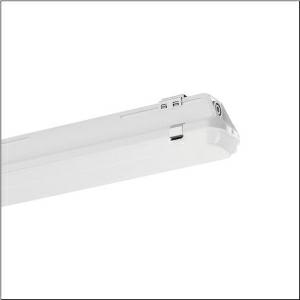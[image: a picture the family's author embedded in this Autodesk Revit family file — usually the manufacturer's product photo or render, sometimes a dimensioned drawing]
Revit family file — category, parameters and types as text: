
# Revit family: monsun_r__21_51fb10dp660b_51d9
name_source: partatom
category: Lighting Fixtures
units: mm (PartAtom-declared; Revit-internal decimal feet)

## family parameters
Cut with Voids When Loaded = No
Host = Face
Light Source = No
Part Type = Normal
Room Calculation Point = No
Round Connector Dimension = Use Diameter
Shared = No

## types (1)
- --- (1 x LED, 6060 lm, 39.4 W, 6500K)
    Apparent Load = 39 VA
    CIE Flux Codes = 47 77 93 94 100
    Color Rendering = 80
    Color Temperature = 6500K
    Default Elevation = 1800 mm
    Description = Monsun® 21, damp-proof luminaire, chain hanger, primary optical cover: enclosure, of PMMA, light emission: direct distribution, primary light characteristic: symmetric, installation type: suspended mounting, surface-mounted, horizontal mounting, vertical mounting, LED, rated luminous flux: 6.060lm, luminous efficacy: 154lm/W, light colour: 865, colour temperature: 6500K, control gear: ECG DALI, with terminal, 5-pole, max. 2.5mm², mains connection: 220..240V, AC, 50/60Hz, rated input power: 39W, housing, of glass-fibre reinforced polyester, uncoated, bright grey, length: 1.590mm, width: 90mm, height: 88mm, clip for enclosure, of stainless steel (V2A), ceiling mounting element, of stainless steel (V2A), chain hanger, of stainless steel (V2A), protection rating (complete): IP66, insulation class (complete): insulation class I (protective earthing), certification: CE, ENEC, VDE, UKCA, protection symbol: D, impact resistance: IK04, permissible operating ambient temperature: -25..+35°C, standard: EN 50419, EN 60598-2-1, corresponds to IFS (International Featured Standards) requirements for safety and quality in the food industry, for indoor or canopied outdoor use, no direct snow, no direct sun, no direct rain, packaging unit: 1 piece
    Height = 89 mm
    Lamp = 1 x LED
    Lamp Light Flux = 6060 lm
    Lamp Power = 39.4 W
    Lamp count = 1
    Length = 1590 mm
    Luminous efficacy = 154 lm/W
    Manufacturer = Siteco
    ModVariant = No
    Model = 51FB10DP660B
    Mounting Place = Ceiling
    Mounting Type = Pendant
    Number of Poles = 1
    OnlyDefault = Yes
    Power Factor = 1
    Product Name = Monsun® 21
    Product group = damp-proof luminaire | ceiling pendant
    ProductGroupID = 908
    Protection Class = Protection class I
    Protection Degree = IP 66
    RLX_Detail_Level = 1
    RlxData = <blob elided: 91765 chars, md5=14f5576d>
    Socket = socket
    Standby Power = 0 W
    System Light Flux = 6060 lm
    System Power = 39 W
    Type Comments = factory setting: luminous flux: 100 % | dim-lin: 254 | 261 mA
    Type Image = l_1006717.jpg
    URL = http://relux.com
    VarID = @adj_125111
    Voltage = 0 V
    Weight = 0.00 kg
    Width = 90 mm

## geometry (parser evidence)
native form markers: Blend x4, Sweep x15
no freeform markers — native parametric forms only
